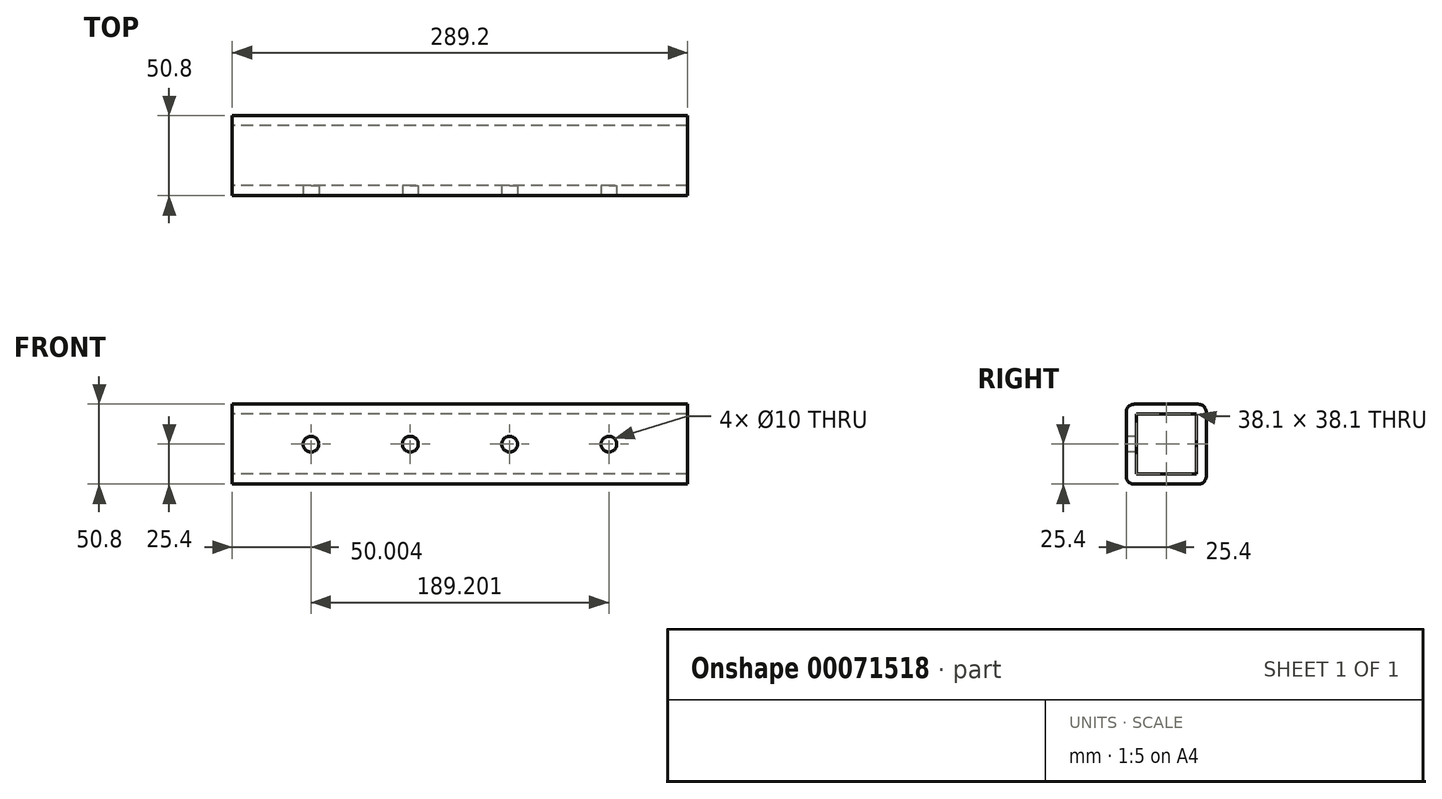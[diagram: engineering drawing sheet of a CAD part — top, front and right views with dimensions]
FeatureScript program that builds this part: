
annotation { "Feature Type Name" : "Feature", "Feature Type Description" : "" }
export const myFeature = defineFeature(function(context is Context, id is Id, definition is map)
    precondition{}
    {
        {
            var Q0;
            Q0=qCreatedBy(makeId("Front.planeOp"),FACE);
            var sketch = newSketch(context, id + "F0", { "sketchPlane" : qUnion([Q0])});
            skLineSegment(sketch, "E0.bottom", {"start": v(-1459.9, 50.8) * mm, "end": v(-1170.7, 50.8) * mm});
            skLineSegment(sketch, "E0.top", {"start": v(-1459.9, 0) * mm, "end": v(-1170.7, 0) * mm});
            skLineSegment(sketch, "E0.left", {"start": v(-1459.9, 50.8) * mm, "end": v(-1459.9, 0) * mm});
            skLineSegment(sketch, "E0.right", {"start": v(-1170.7, 50.8) * mm, "end": v(-1170.7, 0) * mm});
            skSolve(sketch);
        }
        {
            var Q0;
            Q0=qSketchRegion(id+"F0",true);
            extrude(context, id + "F1", {"entities" : qUnion([Q0]), "depth" : 50.8 * mm});
        }
        {
            var Q0;
            Q0=makeQuery(id+"F1.opExtrude","CAP_FACE",FACE,{"disambiguationData":[OSD([sQuery(id+"F0.wireOp",EDGE,"E0.bottom"),sQuery(id+"F0.wireOp",EDGE,"E0.top"),sQuery(id+"F0.wireOp",EDGE,"E0.left"),sQuery(id+"F0.wireOp",EDGE,"E0.right")])],"isStart":false});
            var sketch = newSketch(context, id + "F2", { "sketchPlane" : qUnion([Q0])});
            skCircle(sketch, "E1", {"center": v(-1346.84, 25.4) * mm, "radius": 5 * mm});
            skCircle(sketch, "E2", {"center": v(-1220.7, 25.4) * mm, "radius": 5 * mm});
            skCircle(sketch, "E3", {"center": v(-1283.77, 25.4) * mm, "radius": 5 * mm});
            skCircle(sketch, "E4", {"center": v(-1409.9, 25.4) * mm, "radius": 5 * mm});
            skSolve(sketch);
        }
        {
            var Q0;
            Q0=qSketchRegion(id+"F2",true);
            extrude(context, id + "F3", {"entities" : qUnion([Q0]), "operationType" : NewBodyOperationType.REMOVE, "oppositeDirection" : true, "depth" : 25.4 * mm});
        }
        {
            var Q0;
            Q0=makeQuery(id+"F1.opExtrude","SWEPT_FACE",FACE,{"disambiguationData":[OSD([sQuery(id+"F0.wireOp",EDGE,"E0.left")])]});
            var sketch = newSketch(context, id + "F4", { "sketchPlane" : qUnion([Q0])});
            skLineSegment(sketch, "E5.bottom", {"start": v(6.35, 44.45) * mm, "end": v(44.45, 44.45) * mm});
            skLineSegment(sketch, "E5.top", {"start": v(6.35, 6.35) * mm, "end": v(44.45, 6.35) * mm});
            skLineSegment(sketch, "E5.left", {"start": v(6.35, 44.45) * mm, "end": v(6.35, 6.35) * mm});
            skLineSegment(sketch, "E5.right", {"start": v(44.45, 44.45) * mm, "end": v(44.45, 6.35) * mm});
            skSolve(sketch);
        }
        {
            var Q0;
            Q0=qSketchRegion(id+"F4",true);
            extrude(context, id + "F5", {"entities" : qUnion([Q0]), "operationType" : NewBodyOperationType.REMOVE, "endBound" : BoundingType.THROUGH_ALL, "oppositeDirection" : true, "depth" : 25.4 * mm});
        }
        {
            var Q0;
            Q0=makeQuery(id+"F1.opExtrude","CAP_EDGE",EDGE,{"disambiguationData":[OSD([sQuery(id+"F0.wireOp",EDGE,"E0.bottom")])],"isStart":false});
            var Q1;
            Q1=makeQuery(id+"F1.opExtrude","CAP_EDGE",EDGE,{"disambiguationData":[OSD([sQuery(id+"F0.wireOp",EDGE,"E0.bottom")])],"isStart":true});
            var Q2;
            Q2=makeQuery(id+"F1.opExtrude","CAP_EDGE",EDGE,{"disambiguationData":[OSD([sQuery(id+"F0.wireOp",EDGE,"E0.top")])],"isStart":false});
            var Q3;
            Q3=makeQuery(id+"F1.opExtrude","CAP_EDGE",EDGE,{"disambiguationData":[OSD([sQuery(id+"F0.wireOp",EDGE,"E0.top")])],"isStart":true});
            fillet(context, id + "F6", {"entities" : qUnion([Q0, Q1, Q2, Q3]), "radius" : 5.08 * mm, "tangentPropagation" : true, "allowEdgeOverflow" : false});
        }
    });
